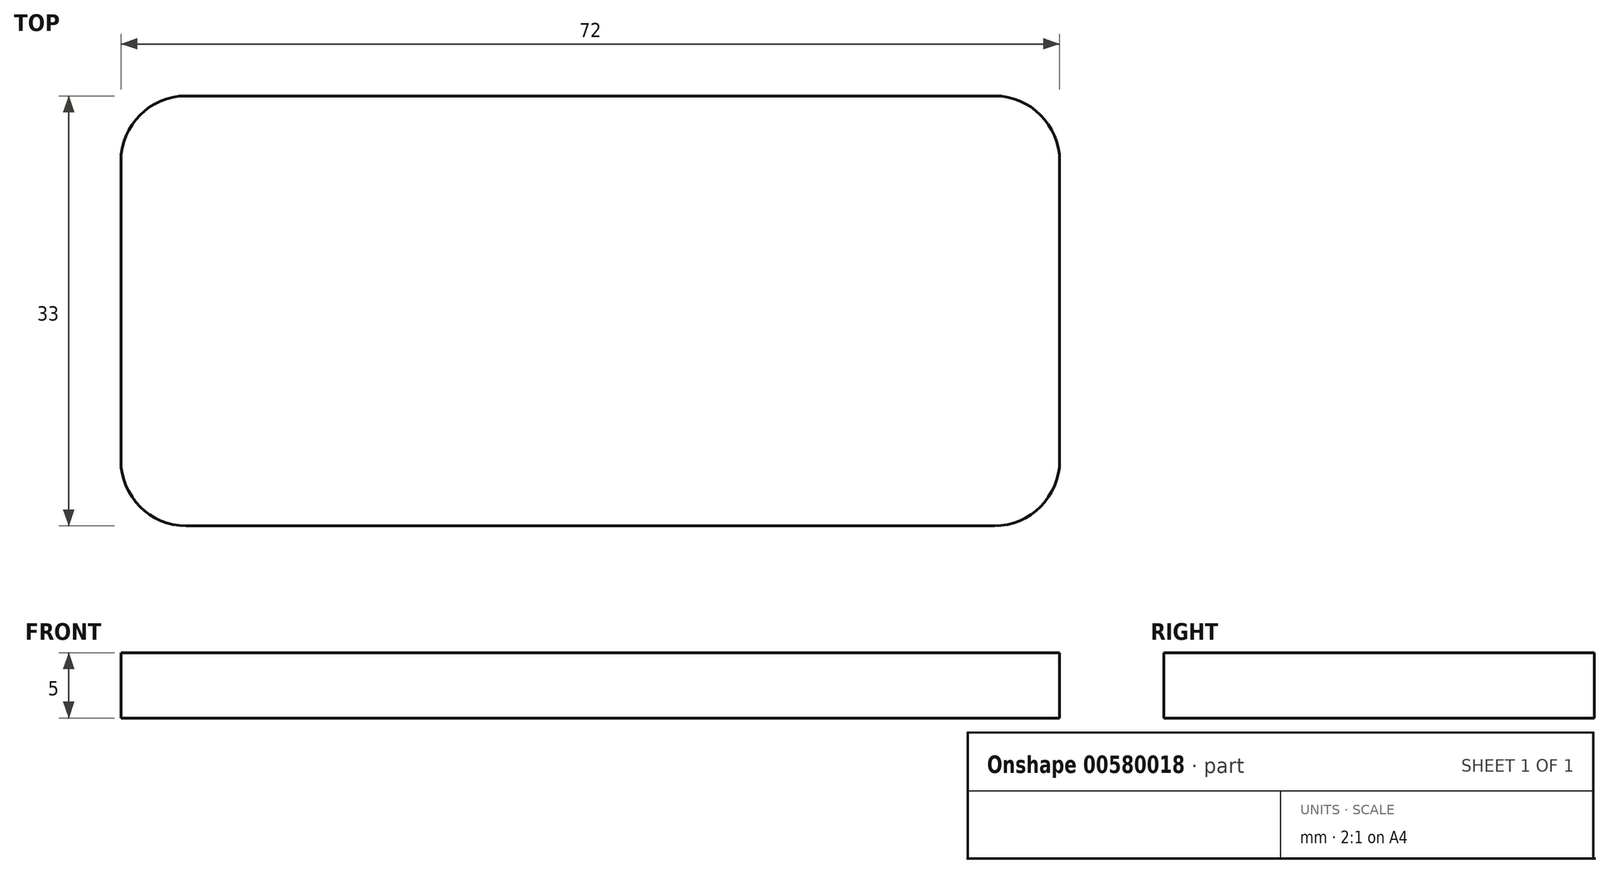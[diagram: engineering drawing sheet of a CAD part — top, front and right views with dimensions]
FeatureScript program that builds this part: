
annotation { "Feature Type Name" : "Feature", "Feature Type Description" : "" }
export const myFeature = defineFeature(function(context is Context, id is Id, definition is map)
    precondition{}
    {
        {
            var Q0;
            Q0=qCreatedBy(makeId("Top.planeOp"),FACE);
            var sketch = newSketch(context, id + "F0", { "sketchPlane" : qUnion([Q0])});
            skLineSegment(sketch, "E0.bottom", {"start": v(5, 0) * mm, "end": v(67, 0) * mm});
            skLineSegment(sketch, "E0.top", {"start": v(5, -33) * mm, "end": v(67, -33) * mm});
            skLineSegment(sketch, "E0.left", {"start": v(0, -5) * mm, "end": v(0, -28) * mm});
            skLineSegment(sketch, "E0.right", {"start": v(72, -5) * mm, "end": v(72, -28) * mm});
            skPoint(sketch, "E1", {"position": v(72, -16.5) * mm});
            skPoint(sketch, "E2.visualSharp", {"position": v(0, 0) * mm});
            skArc(sketch, "E2.filletArc", {"start": v(5, 0) * mm, "mid": v(1.46, -1.46) * mm, "end": v(0, -5) * mm});
            skPoint(sketch, "E3.visualSharp", {"position": v(0, -33) * mm});
            skArc(sketch, "E3.filletArc", {"start": v(0, -28) * mm, "mid": v(1.46, -31.54) * mm, "end": v(5, -33) * mm});
            skPoint(sketch, "E4.visualSharp", {"position": v(72, 0) * mm});
            skArc(sketch, "E4.filletArc", {"start": v(72, -5) * mm, "mid": v(70.54, -1.46) * mm, "end": v(67, 0) * mm});
            skPoint(sketch, "E5.visualSharp", {"position": v(72, -33) * mm});
            skArc(sketch, "E5.filletArc", {"start": v(67, -33) * mm, "mid": v(70.54, -31.54) * mm, "end": v(72, -28) * mm});
            skPoint(sketch, "E6.start.orphan", {"position": v(0, -16.5) * mm});
            skSolve(sketch);
        }
        {
            var Q0;
            Q0 = qSketchRegion(id + "F0", true);
            extrude(context, id + "F1", {"entities" : qUnion([Q0]), "depth" : 5 * mm, "offsetDistance" : 25 * mm});
        }
    });
